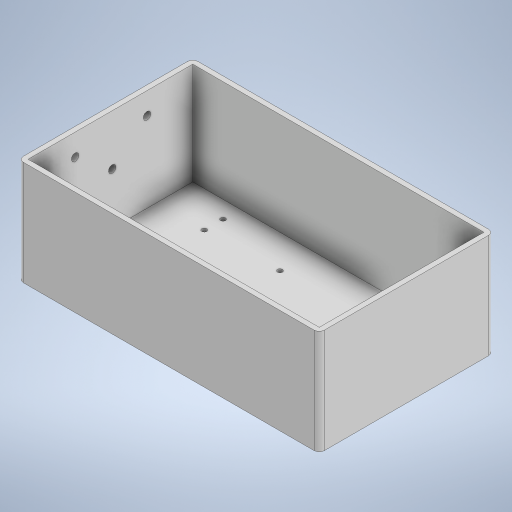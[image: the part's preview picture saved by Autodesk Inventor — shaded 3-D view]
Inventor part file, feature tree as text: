
AUTODESK INVENTOR PART (.ipt)
format: ipt  version: 2023 (Build 270158030, 158C)  size: 512,000 bytes
history: native  units: mm
features: other x4, extrude x4, sketch x4
ambient origin geometry x8: Origin, YZ Plane, XZ Plane, XY Plane, X Axis, Y Axis, Z Axis, Center Point
bodies: Body1 (feature_tree), Body2 (feature_tree)
feature tree (12):
  other  "Kepler_Vibe_XL.iam"
  other  "Die Cast Box.ipt:1"
  other  "Vibe Enclosure"
  extrude  "Extrusion1"  Depth=2.0mm
  extrude  "Extrusion2"  Depth=2.0mm
  extrude  "Extrusion3"  Depth=2.0mm
  extrude  "Extrusion4"  Depth=2.0mm
  sketch  "Sketch1"  dims[d0=10.0mm d1=2.0mm]
  other  "Drill Jig"
  sketch  "Sketch2"  dims[d2=2.0mm d3=2.0mm]
  sketch  "Sketch3"  dims[d4=2.0mm d5=2.0mm]
  sketch  "Sketch4"  dims[d6=2.0mm d7=2.0mm d8=2.0mm d9=2.0mm d10=2.0mm d11=0.0mm d12=2.0mm d13=2.0mm d14=2.0mm d15=2.0mm d16=2.0mm d17=40.0mm d18=0.0mm d19=2.0mm d20=2.0mm d21=2.0mm d22=2.0mm d23=40.0mm d24=-0.261799mm d25=3.0mm d26=3.0mm d27=50.0mm d28=0.0mm]
